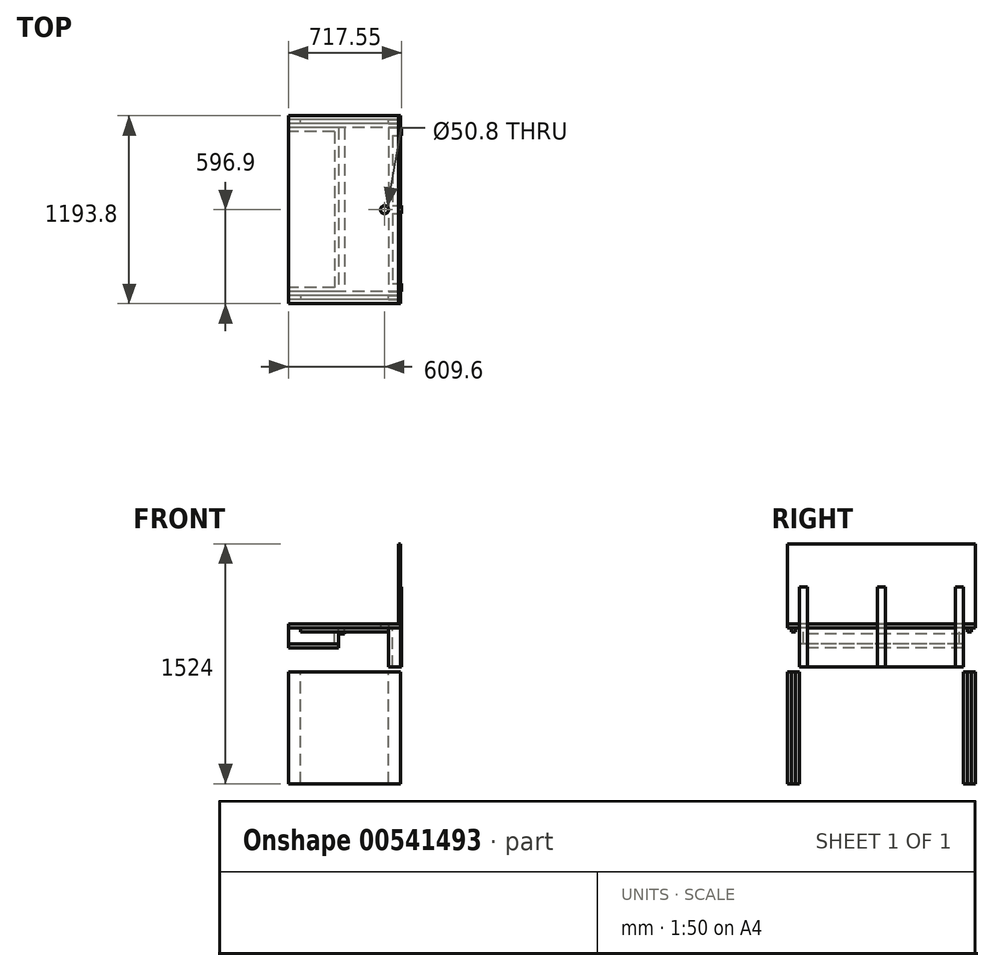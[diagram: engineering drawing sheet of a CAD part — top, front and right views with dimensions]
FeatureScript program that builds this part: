
annotation { "Feature Type Name" : "Feature", "Feature Type Description" : "" }
export const myFeature = defineFeature(function(context is Context, id is Id, definition is map)
    precondition{}
    {
        {
            var Q0;
            Q0=qCreatedBy(makeId("Front.planeOp"),FACE);
            cPlane(context, id + "F0", {"entities" : qUnion([Q0]), "cplaneType" : CPlaneType.OFFSET, "offset" : 571.5 * mm, "width" : 152.4 * mm, "height" : 152.4 * mm});
        }
        {
            var Q0;
            Q0=qCreatedBy(id+"F0.planeOp",FACE);
            var sketch = newSketch(context, id + "F1", { "sketchPlane" : qUnion([Q0])});
            skLineSegment(sketch, "E0.bottom", {"start": v(355.6, -355.6) * mm, "end": v(-355.6, -355.6) * mm});
            skLineSegment(sketch, "E0.top", {"start": v(355.6, 355.6) * mm, "end": v(-355.6, 355.6) * mm});
            skLineSegment(sketch, "E0.left", {"start": v(355.6, -355.6) * mm, "end": v(355.6, 355.6) * mm});
            skLineSegment(sketch, "E0.right", {"start": v(-355.6, -355.6) * mm, "end": v(-355.6, 355.6) * mm});
            skPoint(sketch, "E0.middle", {"position": v(0, 0) * mm});
            skSolve(sketch);
        }
        {
            var Q0;
            Q0 = qSketchRegion(id + "F1", true);
            extrude(context, id + "F2", {"entities" : qUnion([Q0]), "depth" : 25.4 * mm, "offsetDistance" : 25.4 * mm});
        }
        {
            var Q0;
            Q0=qCreatedBy(makeId("Front.planeOp"),FACE);
            cPlane(context, id + "F3", {"entities" : qUnion([Q0]), "cplaneType" : CPlaneType.OFFSET, "offset" : 558.8 * mm, "width" : 152.4 * mm, "height" : 152.4 * mm});
        }
        {
            var Q0;
            Q0=makeQuery(id+"F2.opExtrude","CAP_FACE",FACE,{"disambiguationData":[OSD([sQuery(id+"F1.wireOp",EDGE,"E0.bottom"),sQuery(id+"F1.wireOp",EDGE,"E0.top"),sQuery(id+"F1.wireOp",EDGE,"E0.left"),sQuery(id+"F1.wireOp",EDGE,"E0.right")])],"isStart":true});
            cPlane(context, id + "F4", {"entities" : qUnion([Q0]), "cplaneType" : CPlaneType.OFFSET, "offset" : 0 * mm, "width" : 152.4 * mm, "height" : 152.4 * mm});
        }
        {
            var Q0;
            Q0=qCreatedBy(id+"F4.planeOp",FACE);
            var sketch = newSketch(context, id + "F5", { "sketchPlane" : qUnion([Q0])});
            skLineSegment(sketch, "E1", {"start": v(0, 0) * mm, "end": v(317.5, 0) * mm, "construction": true});
            skLineSegment(sketch, "E2", {"start": v(317.5, 0) * mm, "end": v(355.6, 0) * mm, "construction": true});
            skLineSegment(sketch, "E3", {"start": v(0, 0) * mm, "end": v(-317.5, 0) * mm, "construction": true});
            skLineSegment(sketch, "E4", {"start": v(-317.5, 0) * mm, "end": v(-355.6, 0) * mm, "construction": true});
            skLineSegment(sketch, "E5.bottom", {"start": v(-279.4, -355.6) * mm, "end": v(-355.6, -355.6) * mm});
            skLineSegment(sketch, "E5.top", {"start": v(-279.4, 355.6) * mm, "end": v(-355.6, 355.6) * mm});
            skLineSegment(sketch, "E5.left", {"start": v(-279.4, -355.6) * mm, "end": v(-279.4, 355.6) * mm});
            skLineSegment(sketch, "E5.right", {"start": v(-355.6, -355.6) * mm, "end": v(-355.6, 355.6) * mm});
            skPoint(sketch, "E5.middle", {"position": v(-317.5, 0) * mm});
            skLineSegment(sketch, "E6.bottom", {"start": v(279.4, -355.6) * mm, "end": v(355.6, -355.6) * mm});
            skLineSegment(sketch, "E6.top", {"start": v(279.4, 355.6) * mm, "end": v(355.6, 355.6) * mm});
            skLineSegment(sketch, "E6.left", {"start": v(279.4, -355.6) * mm, "end": v(279.4, 355.6) * mm});
            skLineSegment(sketch, "E6.right", {"start": v(355.6, -355.6) * mm, "end": v(355.6, 355.6) * mm});
            skPoint(sketch, "E6.middle", {"position": v(317.5, 0) * mm});
            skSolve(sketch);
        }
        {
            var Q0;
            Q0=makeQuery(id+"F2.opExtrude","SWEPT_BODY",BODY,{"disambiguationData":[OSD([sQuery(id+"F1.wireOp",EDGE,"E0.bottom"),sQuery(id+"F1.wireOp",EDGE,"E0.top"),sQuery(id+"F1.wireOp",EDGE,"E0.left"),sQuery(id+"F1.wireOp",EDGE,"E0.right")])]});
            var Q1;
            Q1=qCreatedBy(id+"F3.planeOp",FACE);
            mirror(context, id + "F6", {"operationType" : NewBodyOperationType.ADD, "entities" : qUnion([Q0]), "mirrorPlane" : qUnion([Q1])});
        }
        {
            var Q0;
            Q0 = qSketchRegion(id + "F5", true);
            extrude(context, id + "F7", {"entities" : qUnion([Q0]), "depth" : 25.4 * mm, "offsetDistance" : 25.4 * mm});
        }
        {
            var Q0;
            Q0=makeQuery(id+"F2.opExtrude","SWEPT_BODY",BODY,{"disambiguationData":[OSD([sQuery(id+"F1.wireOp",EDGE,"E0.bottom"),sQuery(id+"F1.wireOp",EDGE,"E0.top"),sQuery(id+"F1.wireOp",EDGE,"E0.left"),sQuery(id+"F1.wireOp",EDGE,"E0.right")])]});
            var Q1;
            Q1=makeQuery(id+"F7.opExtrude","SWEPT_BODY",BODY,{"disambiguationData":[OSD([sQuery(id+"F5.wireOp",EDGE,"E5.bottom"),sQuery(id+"F5.wireOp",EDGE,"E5.top"),sQuery(id+"F5.wireOp",EDGE,"E5.left"),sQuery(id+"F5.wireOp",EDGE,"E5.right")])]});
            var Q2;
            Q2=makeQuery(id+"F6.opPattern","COPY",BODY,{"derivedFrom":makeQuery(id+"F2.opExtrude","SWEPT_BODY",BODY,{"disambiguationData":[OSD([sQuery(id+"F1.wireOp",EDGE,"E0.bottom"),sQuery(id+"F1.wireOp",EDGE,"E0.top"),sQuery(id+"F1.wireOp",EDGE,"E0.left"),sQuery(id+"F1.wireOp",EDGE,"E0.right")])]}),"instanceName":"1"});
            var Q3;
            Q3=makeQuery(id+"F7.opExtrude","SWEPT_BODY",BODY,{"disambiguationData":[OSD([sQuery(id+"F5.wireOp",EDGE,"E6.bottom"),sQuery(id+"F5.wireOp",EDGE,"E6.top"),sQuery(id+"F5.wireOp",EDGE,"E6.left"),sQuery(id+"F5.wireOp",EDGE,"E6.right")])]});
            var Q4;
            Q4=qCreatedBy(makeId("Front.planeOp"),FACE);
            mirror(context, id + "F8", {"entities" : qUnion([Q0, Q1, Q2, Q3]), "mirrorPlane" : qUnion([Q4])});
        }
        {
            var Q0;
            Q0=qCreatedBy(makeId("Top.planeOp"),FACE);
            cPlane(context, id + "F9", {"entities" : qUnion([Q0]), "cplaneType" : CPlaneType.OFFSET, "offset" : 635 * mm, "width" : 152.4 * mm, "height" : 152.4 * mm});
        }
        {
            var Q0;
            Q0=qCreatedBy(id+"F9.planeOp",FACE);
            var sketch = newSketch(context, id + "F10", { "sketchPlane" : qUnion([Q0])});
            skLineSegment(sketch, "E7", {"start": v(0, 0) * mm, "end": v(0, 558.8) * mm, "construction": true});
            skLineSegment(sketch, "E8", {"start": v(0, 0) * mm, "end": v(0, -558.8) * mm, "construction": true});
            skLineSegment(sketch, "E9.bottom", {"start": v(279.4, -571.5) * mm, "end": v(-279.4, -571.5) * mm});
            skLineSegment(sketch, "E9.top", {"start": v(279.4, -546.1) * mm, "end": v(-279.4, -546.1) * mm});
            skLineSegment(sketch, "E9.left", {"start": v(279.4, -571.5) * mm, "end": v(279.4, -546.1) * mm});
            skLineSegment(sketch, "E9.right", {"start": v(-279.4, -571.5) * mm, "end": v(-279.4, -546.1) * mm});
            skPoint(sketch, "E9.middle", {"position": v(0, -558.8) * mm});
            skPoint(sketch, "E10.middle", {"position": v(0, 558.8) * mm});
            skLineSegment(sketch, "E11.bottom", {"start": v(279.4, 546.1) * mm, "end": v(-279.4, 546.1) * mm});
            skLineSegment(sketch, "E11.top", {"start": v(279.4, 571.5) * mm, "end": v(-279.4, 571.5) * mm});
            skLineSegment(sketch, "E11.left", {"start": v(279.4, 546.1) * mm, "end": v(279.4, 571.5) * mm});
            skLineSegment(sketch, "E11.right", {"start": v(-279.4, 546.1) * mm, "end": v(-279.4, 571.5) * mm});
            skSolve(sketch);
        }
        {
            var Q0;
            Q0 = qSketchRegion(id + "F10", true);
            extrude(context, id + "F11", {"entities" : qUnion([Q0]), "oppositeDirection" : true, "depth" : 25.4 * mm, "offsetDistance" : 25.4 * mm});
        }
        {
            var Q0;
            Q0=makeQuery(id+"F11.opExtrude","CAP_FACE",FACE,{"disambiguationData":[OSD([sQuery(id+"F10.wireOp",EDGE,"E11.bottom"),sQuery(id+"F10.wireOp",EDGE,"E11.top"),sQuery(id+"F10.wireOp",EDGE,"E11.left"),sQuery(id+"F10.wireOp",EDGE,"E11.right")])],"isStart":true});
            var sketch = newSketch(context, id + "F12", { "sketchPlane" : qUnion([Q0])});
            skPoint(sketch, "E12.firstSnap0", {"position": v(-373.26, 754.03) * mm});
            skLineSegment(sketch, "E12.bottom", {"start": v(-355.6, 596.9) * mm, "end": v(355.6, 596.9) * mm});
            skLineSegment(sketch, "E12.top", {"start": v(-355.6, -596.9) * mm, "end": v(355.6, -596.9) * mm});
            skLineSegment(sketch, "E12.left", {"start": v(-355.6, 596.9) * mm, "end": v(-355.6, -596.9) * mm});
            skLineSegment(sketch, "E12.right", {"start": v(355.6, 596.9) * mm, "end": v(355.6, -596.9) * mm});
            skLineSegment(sketch, "E13", {"start": v(0, 546.1) * mm, "end": v(0, 596.9) * mm, "construction": true});
            skLineSegment(sketch, "E14", {"start": v(0, 546.1) * mm, "end": v(355.6, 546.1) * mm, "construction": true});
            skLineSegment(sketch, "E15", {"start": v(355.6, 0) * mm, "end": v(254, 0) * mm, "construction": true});
            skPoint(sketch, "E15.endSnap0", {"position": v(355.6, 0) * mm});
            skCircle(sketch, "E16", {"center": v(254, 0) * mm, "radius": 25.4 * mm});
            skSolve(sketch);
        }
        {
            var Q0;
            Q0 = qSketchRegion(id + "F12", true);
            extrude(context, id + "F13", {"entities" : qUnion([Q0]), "operationType" : NewBodyOperationType.ADD, "depth" : 25.4 * mm, "offsetDistance" : 25.4 * mm});
        }
        {
            var Q0;
            Q0=makeQuery(id+"F13.opExtrude","CAP_FACE",FACE,{"disambiguationData":[OSD([sQuery(id+"F12.wireOp",EDGE,"E12.bottom"),sQuery(id+"F12.wireOp",EDGE,"E12.top"),sQuery(id+"F12.wireOp",EDGE,"E12.left"),sQuery(id+"F12.wireOp",EDGE,"E12.right")])],"isStart":true});
            var sketch = newSketch(context, id + "F14", { "sketchPlane" : qUnion([Q0])});
            skLineSegment(sketch, "E17", {"start": v(-355.6, 0) * mm, "end": v(-50.8, 0) * mm});
            skLineSegment(sketch, "E18.bottom", {"start": v(-38.1, -520.7) * mm, "end": v(-63.5, -520.7) * mm});
            skLineSegment(sketch, "E18.top", {"start": v(-38.1, 520.7) * mm, "end": v(-63.5, 520.7) * mm});
            skLineSegment(sketch, "E18.left", {"start": v(-38.1, -520.7) * mm, "end": v(-38.1, 520.7) * mm});
            skLineSegment(sketch, "E18.right", {"start": v(-63.5, -520.7) * mm, "end": v(-63.5, 520.7) * mm});
            skPoint(sketch, "E18.middle", {"position": v(-50.8, 0) * mm});
            skLineSegment(sketch, "E19.bottom", {"start": v(-63.5, 520.7) * mm, "end": v(-355.6, 520.7) * mm});
            skLineSegment(sketch, "E19.top", {"start": v(-63.5, 495.3) * mm, "end": v(-355.6, 495.3) * mm});
            skLineSegment(sketch, "E19.left", {"start": v(-63.5, 520.7) * mm, "end": v(-63.5, 495.3) * mm});
            skLineSegment(sketch, "E19.right", {"start": v(-355.6, 520.7) * mm, "end": v(-355.6, 495.3) * mm});
            skLineSegment(sketch, "E20.bottom", {"start": v(-63.5, -520.7) * mm, "end": v(-355.6, -520.7) * mm});
            skLineSegment(sketch, "E20.top", {"start": v(-63.5, -495.3) * mm, "end": v(-355.6, -495.3) * mm});
            skLineSegment(sketch, "E20.left", {"start": v(-63.5, -520.7) * mm, "end": v(-63.5, -495.3) * mm});
            skLineSegment(sketch, "E20.right", {"start": v(-355.6, -520.7) * mm, "end": v(-355.6, -495.3) * mm});
            skSolve(sketch);
        }
        {
            var Q0;
            Q0 = qSketchRegion(id + "F14", true);
            extrude(context, id + "F15", {"entities" : qUnion([Q0]), "depth" : 101.6 * mm, "offsetDistance" : 25.4 * mm});
        }
        {
            var Q0;
            Q0=makeQuery(id+"F15.opExtrude","CAP_FACE",FACE,{"disambiguationData":[OSD([sQuery(id+"F14.wireOp",EDGE,"E18.bottom"),sQuery(id+"F14.wireOp",EDGE,"E18.top"),sQuery(id+"F14.wireOp",EDGE,"E18.left"),sQuery(id+"F14.wireOp",EDGE,"E18.right"),sQuery(id+"F14.wireOp",EDGE,"E19.bottom"),sQuery(id+"F14.wireOp",EDGE,"E19.top"),sQuery(id+"F14.wireOp",EDGE,"E19.right"),sQuery(id+"F14.wireOp",EDGE,"E20.bottom"),sQuery(id+"F14.wireOp",EDGE,"E20.top"),sQuery(id+"F14.wireOp",EDGE,"E20.right")])],"isStart":false});
            var sketch = newSketch(context, id + "F16", { "sketchPlane" : qUnion([Q0])});
            skLineSegment(sketch, "E21", {"start": v(-63.5, 0) * mm, "end": v(-196.85, 0) * mm, "construction": true});
            skPoint(sketch, "E21.endSnap0", {"position": v(-196.85, -520.7) * mm});
            skLineSegment(sketch, "E22", {"start": v(-196.85, 0) * mm, "end": v(-196.85, -520.7) * mm, "construction": true});
            skLineSegment(sketch, "E23.bottom", {"start": v(-38.1, -520.7) * mm, "end": v(-355.6, -520.7) * mm});
            skLineSegment(sketch, "E23.top", {"start": v(-38.1, 520.7) * mm, "end": v(-355.6, 520.7) * mm});
            skLineSegment(sketch, "E23.left", {"start": v(-38.1, -520.7) * mm, "end": v(-38.1, 520.7) * mm});
            skLineSegment(sketch, "E23.right", {"start": v(-355.6, -520.7) * mm, "end": v(-355.6, 520.7) * mm});
            skPoint(sketch, "E23.middle", {"position": v(-196.85, 0) * mm});
            skSolve(sketch);
        }
        {
            var Q0;
            Q0 = qSketchRegion(id + "F16", true);
            extrude(context, id + "F17", {"entities" : qUnion([Q0]), "depth" : 25.4 * mm, "offsetDistance" : 25.4 * mm});
        }
        {
            var Q0;
            Q0=makeQuery(id+"F13.opExtrude","CAP_FACE",FACE,{"disambiguationData":[OSD([sQuery(id+"F12.wireOp",EDGE,"E12.bottom"),sQuery(id+"F12.wireOp",EDGE,"E12.top"),sQuery(id+"F12.wireOp",EDGE,"E12.left"),sQuery(id+"F12.wireOp",EDGE,"E12.right")])],"isStart":true});
            var sketch = newSketch(context, id + "F18", { "sketchPlane" : qUnion([Q0])});
            skLineSegment(sketch, "E24", {"start": v(355.6, 0) * mm, "end": v(292.1, 0) * mm, "construction": true});
            skLineSegment(sketch, "E25", {"start": v(292.1, 0) * mm, "end": v(292.1, 520.7) * mm, "construction": true});
            skLineSegment(sketch, "E26.bottom", {"start": v(279.4, -520.7) * mm, "end": v(304.8, -520.7) * mm});
            skLineSegment(sketch, "E26.top", {"start": v(279.4, 520.7) * mm, "end": v(304.8, 520.7) * mm});
            skLineSegment(sketch, "E26.left", {"start": v(279.4, -520.7) * mm, "end": v(279.4, 520.7) * mm});
            skLineSegment(sketch, "E26.right", {"start": v(304.8, -520.7) * mm, "end": v(304.8, 520.7) * mm});
            skPoint(sketch, "E26.middle", {"position": v(292.1, 0) * mm});
            skLineSegment(sketch, "E27.bottom", {"start": v(304.8, 520.7) * mm, "end": v(355.6, 520.7) * mm});
            skLineSegment(sketch, "E27.top", {"start": v(304.8, 469.9) * mm, "end": v(355.6, 469.9) * mm});
            skLineSegment(sketch, "E27.left", {"start": v(304.8, 520.7) * mm, "end": v(304.8, 469.9) * mm});
            skLineSegment(sketch, "E27.right", {"start": v(355.6, 520.7) * mm, "end": v(355.6, 469.9) * mm});
            skLineSegment(sketch, "E28.bottom", {"start": v(304.8, -520.7) * mm, "end": v(355.6, -520.7) * mm});
            skLineSegment(sketch, "E28.top", {"start": v(304.8, -469.9) * mm, "end": v(355.6, -469.9) * mm});
            skLineSegment(sketch, "E28.left", {"start": v(304.8, -520.7) * mm, "end": v(304.8, -469.9) * mm});
            skLineSegment(sketch, "E28.right", {"start": v(355.6, -520.7) * mm, "end": v(355.6, -469.9) * mm});
            skPoint(sketch, "E29", {"position": v(304.8, 25.4) * mm});
            skPoint(sketch, "E30", {"position": v(304.8, 0) * mm});
            skLineSegment(sketch, "E31.bottom", {"start": v(304.8, 25.4) * mm, "end": v(355.6, 25.4) * mm});
            skLineSegment(sketch, "E31.top", {"start": v(304.8, -25.4) * mm, "end": v(355.6, -25.4) * mm});
            skLineSegment(sketch, "E31.left", {"start": v(304.8, 25.4) * mm, "end": v(304.8, -25.4) * mm});
            skLineSegment(sketch, "E31.right", {"start": v(355.6, 25.4) * mm, "end": v(355.6, -25.4) * mm});
            skSolve(sketch);
        }
        {
            var Q0;
            Q0 = qSketchRegion(id + "F18", true);
            extrude(context, id + "F19", {"entities" : qUnion([Q0]), "depth" : 250 * mm, "offsetDistance" : 25.4 * mm});
        }
        {
            var Q0;
            Q0=makeQuery(id+"F13.opExtrude","SWEPT_FACE",FACE,{"disambiguationData":[OSD([sQuery(id+"F12.wireOp",EDGE,"E12.right")])]});
            var sketch = newSketch(context, id + "F20", { "sketchPlane" : qUnion([Q0])});
            skLineSegment(sketch, "E32.bottom", {"start": v(-596.9, 660.4) * mm, "end": v(596.9, 660.4) * mm});
            skLineSegment(sketch, "E32.top", {"start": v(-596.9, 1168.4) * mm, "end": v(596.9, 1168.4) * mm});
            skLineSegment(sketch, "E32.left", {"start": v(-596.9, 660.4) * mm, "end": v(-596.9, 1168.4) * mm});
            skLineSegment(sketch, "E32.right", {"start": v(596.9, 660.4) * mm, "end": v(596.9, 1168.4) * mm});
            skSolve(sketch);
        }
        {
            var Q0;
            Q0 = qSketchRegion(id + "F20", true);
            extrude(context, id + "F21", {"entities" : qUnion([Q0]), "oppositeDirection" : true, "depth" : 12.7 * mm, "offsetDistance" : 25.4 * mm});
        }
        {
            var Q0;
            Q0=makeQuery(id+"F19.opExtrude","SWEPT_FACE",FACE,{"disambiguationData":[OSD([sQuery(id+"F18.wireOp",EDGE,"E31.right")])]});
            var sketch = newSketch(context, id + "F22", { "sketchPlane" : qUnion([Q0])});
            skLineSegment(sketch, "E33.bottom", {"start": v(-25.4, 385) * mm, "end": v(25.4, 385) * mm});
            skLineSegment(sketch, "E33.top", {"start": v(-25.4, 893) * mm, "end": v(25.4, 893) * mm});
            skLineSegment(sketch, "E33.left", {"start": v(-25.4, 385) * mm, "end": v(-25.4, 893) * mm});
            skLineSegment(sketch, "E33.right", {"start": v(25.4, 385) * mm, "end": v(25.4, 893) * mm});
            skLineSegment(sketch, "E34", {"start": v(25.4, 385) * mm, "end": v(469.9, 385) * mm, "construction": true});
            skLineSegment(sketch, "E35", {"start": v(-25.4, 385) * mm, "end": v(-469.9, 385) * mm, "construction": true});
            skLineSegment(sketch, "E36.bottom", {"start": v(469.9, 385) * mm, "end": v(520.7, 385) * mm});
            skLineSegment(sketch, "E36.top", {"start": v(469.9, 893) * mm, "end": v(520.7, 893) * mm});
            skLineSegment(sketch, "E36.left", {"start": v(469.9, 385) * mm, "end": v(469.9, 893) * mm});
            skLineSegment(sketch, "E36.right", {"start": v(520.7, 385) * mm, "end": v(520.7, 893) * mm});
            skLineSegment(sketch, "E37.bottom", {"start": v(-469.9, 385) * mm, "end": v(-520.7, 385) * mm});
            skLineSegment(sketch, "E37.top", {"start": v(-469.9, 893) * mm, "end": v(-520.7, 893) * mm});
            skLineSegment(sketch, "E37.left", {"start": v(-469.9, 385) * mm, "end": v(-469.9, 893) * mm});
            skLineSegment(sketch, "E37.right", {"start": v(-520.7, 385) * mm, "end": v(-520.7, 893) * mm});
            skSolve(sketch);
        }
        {
            var Q0;
            Q0 = qSketchRegion(id + "F22", true);
            extrude(context, id + "F23", {"entities" : qUnion([Q0]), "depth" : 6.35 * mm, "offsetDistance" : 25.4 * mm});
        }
        {
            var Q0;
            Q0=makeQuery(id+"F13.opExtrude","CAP_FACE",FACE,{"disambiguationData":[OSD([sQuery(id+"F12.wireOp",EDGE,"E12.bottom"),sQuery(id+"F12.wireOp",EDGE,"E12.top"),sQuery(id+"F12.wireOp",EDGE,"E12.left"),sQuery(id+"F12.wireOp",EDGE,"E12.right"),sQuery(id+"F12.wireOp",EDGE,"E16")])],"isStart":true});
            var sketch = newSketch(context, id + "F24", { "sketchPlane" : qUnion([Q0])});
            skLineSegment(sketch, "E38", {"start": v(0, 0) * mm, "end": v(-19.05, 0) * mm, "construction": true});
            skLineSegment(sketch, "E39", {"start": v(-19.05, 0) * mm, "end": v(-38.1, 0) * mm, "construction": true});
            skLineSegment(sketch, "E40.bottom", {"start": v(0, -520.7) * mm, "end": v(-38.1, -520.7) * mm});
            skLineSegment(sketch, "E40.top", {"start": v(0, 520.7) * mm, "end": v(-38.1, 520.7) * mm});
            skLineSegment(sketch, "E40.left", {"start": v(0, -520.7) * mm, "end": v(0, 520.7) * mm});
            skLineSegment(sketch, "E40.right", {"start": v(-38.1, -520.7) * mm, "end": v(-38.1, 520.7) * mm});
            skPoint(sketch, "E40.middle", {"position": v(-19.05, 0) * mm});
            skSolve(sketch);
        }
        {
            var Q0;
            Q0 = qSketchRegion(id + "F24", true);
            extrude(context, id + "F25", {"entities" : qUnion([Q0]), "depth" : 38.1 * mm, "offsetDistance" : 25.4 * mm});
        }
    });
